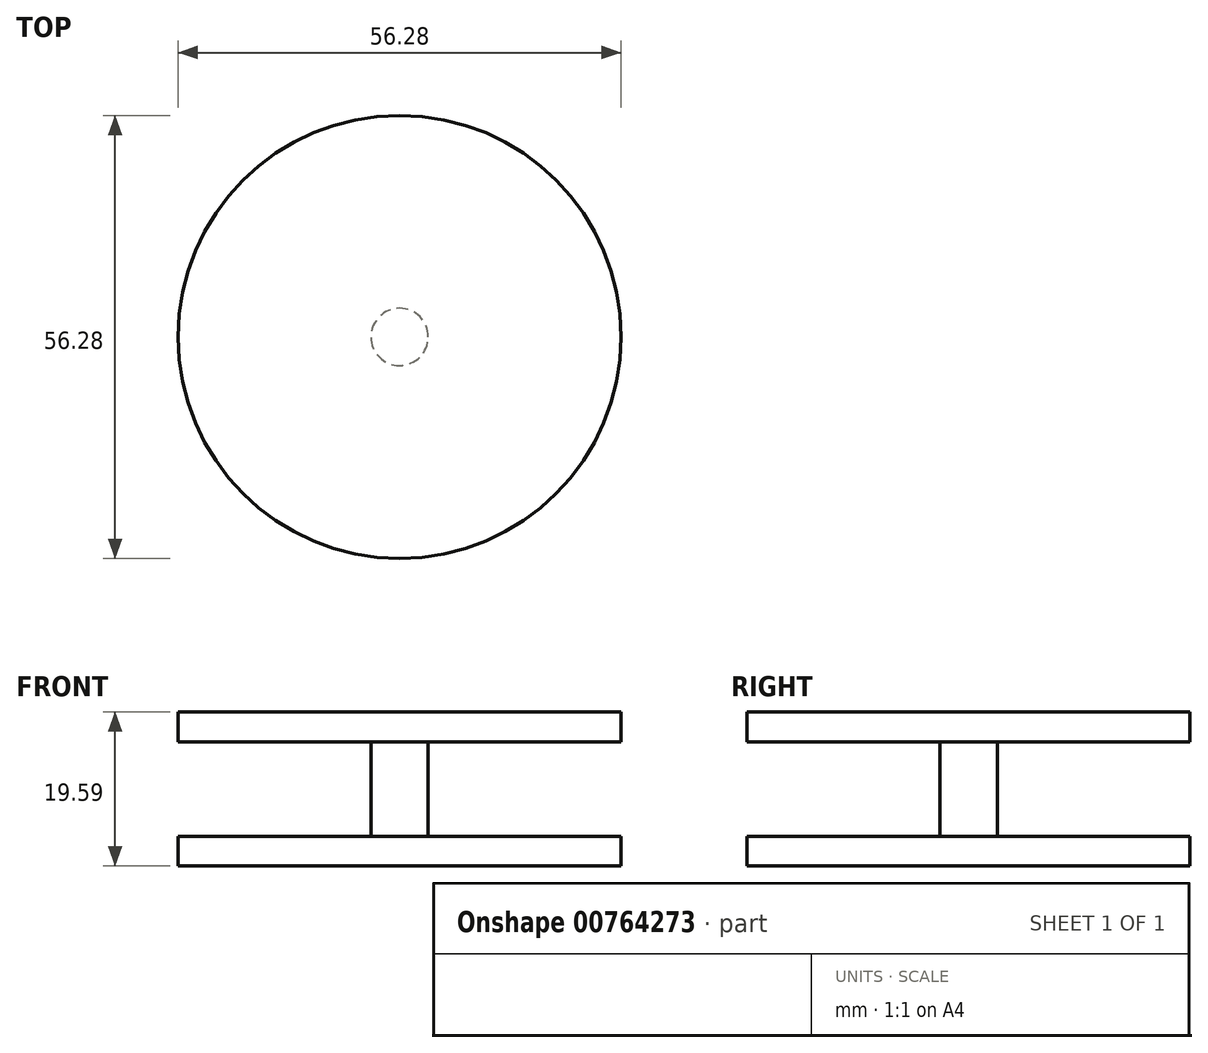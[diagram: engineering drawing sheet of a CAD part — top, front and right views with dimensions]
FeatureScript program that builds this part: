
annotation { "Feature Type Name" : "Feature", "Feature Type Description" : "" }
export const myFeature = defineFeature(function(context is Context, id is Id, definition is map)
    precondition{}
    {
        {
            var Q0;
            Q0=qCreatedBy(makeId("Right.planeOp"),FACE);
            var sketch = newSketch(context, id + "F0", { "sketchPlane" : qUnion([Q0])});
            skLineSegment(sketch, "E0", {"start": v(0, 0) * mm, "end": v(0, 19.59) * mm});
            skLineSegment(sketch, "E1", {"start": v(0, 19.59) * mm, "end": v(28.14, 19.59) * mm});
            skLineSegment(sketch, "E2", {"start": v(28.14, 19.59) * mm, "end": v(28.14, 15.76) * mm});
            skLineSegment(sketch, "E3", {"start": v(28.14, 15.76) * mm, "end": v(3.64, 15.76) * mm});
            skLineSegment(sketch, "E4", {"start": v(3.64, 15.76) * mm, "end": v(3.64, 3.76) * mm});
            skLineSegment(sketch, "E5", {"start": v(3.64, 3.76) * mm, "end": v(28.14, 3.76) * mm});
            skLineSegment(sketch, "E6", {"start": v(28.14, 3.76) * mm, "end": v(28.14, 0) * mm});
            skLineSegment(sketch, "E7", {"start": v(28.14, 0) * mm, "end": v(0, 0) * mm});
            skSolve(sketch);
        }
        {
            var Q0;
            Q0=makeQuery(id+"F0.imprint","IMPRINT",FACE,{"disambiguationData":[TD([[makeQuery(id+"F0.imprint","IMPRINT",EDGE,{"derivedFrom":sQuery(id+"F0.wireOp",EDGE,"E0")}),-1.0]])]});
            var Q1;
            Q1=sQuery(id+"F0.wireOp",EDGE,"E0");
            revolve(context, id + "F1", {"surfaceOperationType" : NewSurfaceOperationType.NEW, "entities" : qUnion([Q0]), "axis" : qUnion([Q1]), "revolveType" : RevolveType.FULL});
        }
    });
